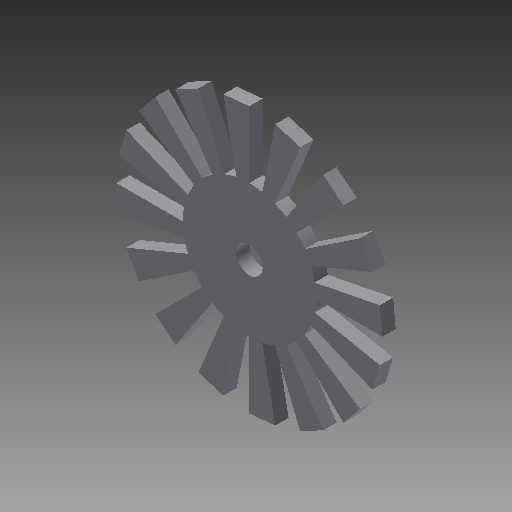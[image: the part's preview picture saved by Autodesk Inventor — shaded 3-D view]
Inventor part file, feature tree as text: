
AUTODESK INVENTOR PART (.ipt)
format: ipt  version: 2017 (Build 210142000, 142)  size: 181,248 bytes
history: native  units: in
note: dims shown in document units (in); Inventor stores cm internally (conversion verified against a paired STEP export)
features: other x3, sketch x1
ambient origin geometry x8: Origin, YZ Plane, XZ Plane, XY Plane, X Axis, Y Axis, Z Axis, Center Point
bodies: Solid1 (feature_tree)
feature tree (4):
  other  "encoder_MIR4.ipt"
  other  "Solid1::encoder_MIR4.ipt"
  other  "TaggingFeature1"
  sketch  "Sketch1"  dims[d0=0.3937in]
